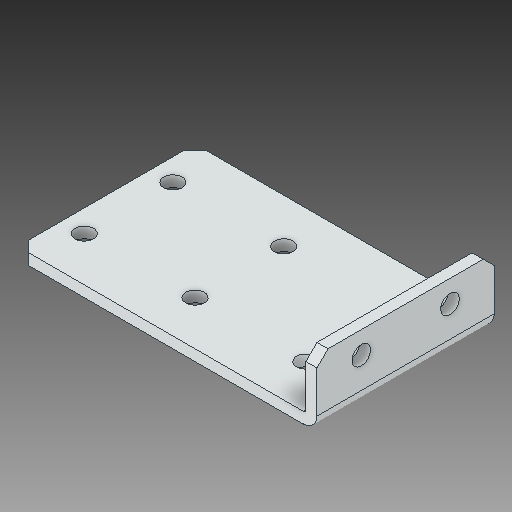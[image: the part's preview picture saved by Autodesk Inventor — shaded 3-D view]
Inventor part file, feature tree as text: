
AUTODESK INVENTOR PART (.ipt)
format: ipt  version: 2018.2 (Build 222227000, 227)  size: 110,592 bytes
history: native  units: in
note: dims shown in document units (in); Inventor stores cm internally (conversion verified against a paired STEP export)
features: chamfer x1
ambient origin geometry x8: Origin, YZ Plane, XZ Plane, XY Plane, X Axis, Y Axis, Z Axis, Center Point
bodies: Solid1 (feature_tree)
feature tree (1):
  chamfer  "Chamfer2"  [1 undecoded]
note: 1 required parameter value undecoded (feature->parameter linkage not recoverable at this tier; creation-order binding heuristic only, values carry confidence <= 0.55)
